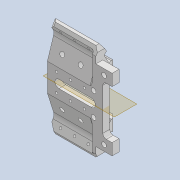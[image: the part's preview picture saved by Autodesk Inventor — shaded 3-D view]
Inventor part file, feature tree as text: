
AUTODESK INVENTOR PART (.ipt)
format: ipt  version: 2020 (Build 240168000, 168)  size: 567,808 bytes
history: native  units: mm
features: reference x17, projected_geometry x17, sketch x14, extrude x12, thicken_offset x7, fillet x7, other x5, mirror x4, plane x3, chamfer x3, hole x2
ambient origin geometry x8: Origin, YZ Plane, XZ Plane, XY Plane, X Axis, Y Axis, Z Axis, Center Point
bodies: Solid1 (feature_tree)
feature tree (91):
  sketch  "Sketch1"  dims[d0=5.0mm d1=7.0mm]
  plane  "Work Plane1"
  extrude  "Extrusion1"  Depth=7.0mm
  sketch  "Sketch2"  dims[d2=5.0mm d3=7.0mm]
  plane  "Work Plane2"
  extrude  "Extrusion2"  Depth=7.0mm
  hole  "Hole1"  [1 undecoded]
  plane  "Work Plane3"
  mirror  "Mirror1"
  extrude  "Extrusion3"  Depth=10.0mm
  thicken_offset  "Thicken1"
  thicken_offset  "Thicken2"
  thicken_offset  "Thicken3"
  extrude  "Extrusion4"  Depth=10.0mm
  extrude  "Extrusion5"  Depth=20.0mm TaperAngle=0.0deg
  thicken_offset  "Thicken4"
  thicken_offset  "Thicken5"
  extrude  "Extrusion6"  Depth=1.0mm
  extrude  "Extrusion7"  Depth=1.0mm
  fillet  "Fillet2"  Radius=1.0mm
  fillet  "Fillet3"  Radius=1.0mm
  fillet  "Fillet4"  Radius=2.9mm
  thicken_offset  "Thicken6"
  thicken_offset  "Thicken7"
  fillet  "Fillet5"  Radius=1.45mm
  chamfer  "Chamfer1"  Distance=21.5mm
  extrude  "Extrusion8"  Depth=1.0mm
  fillet  "Fillet6"  Radius=1.0mm
  chamfer  "Chamfer2"  Distance=20.0mm
  extrude  "Extrusion9"  Depth=1.5mm
  fillet  "Fillet7"  Radius=0.5mm
  mirror  "Mirror2"
  hole  "Hole2"  [1 undecoded]
  extrude  "Extrusion10"  Depth=1.5mm TaperAngle=0.0deg
  extrude  "Extrusion11"  Depth=0.1mm TaperAngle=0.0deg
  mirror  "Mirror3"
  extrude  "Extrusion12"  Depth=0.4mm
  mirror  "Mirror4"
  chamfer  "Chamfer3"  Distance=0.6mm
  fillet  "Fillet8"  Radius=1.0mm
  reference  "Reference1"
  reference  "Reference2"
  reference  "Reference3"
  reference  "Reference4"
  reference  "Reference5"
  reference  "Reference6"
  reference  "Reference7"
  reference  "Reference8"
  reference  "Reference9"
  reference  "Reference10"
  reference  "Reference11"
  reference  "Reference12"
  reference  "Reference13"
  reference  "Reference14"
  projected_geometry  "Projected Loop1"
  sketch  "Sketch3"  dims[d4=3.0mm d5=21.0mm]
  reference  "Reference15"
  reference  "Reference16"
  reference  "Reference17"
  sketch  "Sketch4"  dims[d6=10.0mm d7=0.0mm d8=2.0mm]
  projected_geometry  "Projected Loop2"
  projected_geometry  "Projected Loop3"
  sketch  "Sketch5"  dims[d9=10.0mm d10=0.0mm]
  projected_geometry  "Projected Loop4"
  sketch  "Sketch6"  dims[d11=1.1mm d12=6.0mm d13=4.0mm d14=2.0mm d15=90.0deg d16=10.0mm d17=0.0mm d18=2.0mm]
  projected_geometry  "Projected Loop5"
  projected_geometry  "Projected Loop6"
  projected_geometry  "Projected Loop7"
  sketch  "Sketch7"  dims[d19=2.0mm d20=20.0mm d21=0.0mm]
  projected_geometry  "Projected Loop8"
  projected_geometry  "Projected Loop9"
  sketch  "Sketch8"  dims[d22=1.0mm d23=1.0mm]
  projected_geometry  "Projected Loop10"
  sketch  "Sketch9"  dims[d24=1.0mm d25=1.0mm d26=1.0mm d27=1.0mm d28=2.9mm d29=1.45mm]
  projected_geometry  "Projected Loop11"
  projected_geometry  "Projected Loop12"
  sketch  "Sketch10"  dims[d30=2.9mm]
  projected_geometry  "Projected Loop13"
  sketch  "Sketch11"  dims[d31=12.0mm d32=21.5mm d33=0.0mm]
  projected_geometry  "Projected Loop14"
  sketch  "Sketch12"  dims[d35=1.0mm d36=1.0mm d37=1.0mm]
  projected_geometry  "Projected Loop15"
  sketch  "Sketch13"  dims[d38=1.0mm d39=20.0mm d40=0.0mm]
  projected_geometry  "Projected Loop16"
  sketch  "Sketch14"  dims[d41=0.5mm d42=0.5mm d43=0.5mm d44=0.5mm d45=20.0mm d46=0.0mm d47=0.1mm d48=0.0mm d49=0.4mm d50=0.6mm d51=1.0mm d52=0.5mm d53=0.5mm d54=0.5mm d55=0.5mm d56=3.0mm d57=1.5mm d58=2.0mm d59=45.0deg d60=2.0mm d61=0.0mm d62=1.0mm d63=1.5mm d64=2.0mm d65=45.0deg d66=3.5mm d67=3.5mm d68=1.5mm d69=30.0mm d70=0.0mm d71=1.0mm d72=4.0mm d73=6.0mm d74=6.0mm d75=4.0mm d76=4.0mm d77=4.0mm d78=4.0mm d79=4.0mm d80=4.0mm d81=1.1mm d82=6.0mm d83=4.0mm d84=2.0mm d85=90.0deg d86=10.0mm d87=0.0mm d88=7.0mm d89=3.5mm d90=30.0mm d91=0.0mm d92=4.0mm d93=1.0mm d94=2.0mm d95=30.0mm d96=0.0mm d97=5.0mm d98=8.0mm d99=2.0mm d100=2.0mm d101=30.0mm d102=0.0mm d103=2.0mm d104=2.0mm d105=45.0deg d106=1.5mm]
  projected_geometry  "Projected Loop17"
  parser-record x1  (decoder bookkeeping rows leaked as tree rows — omitted from the tree; the rows remain in map.json)
  other  "tip_3_n_ass.iam"
  other  "end_shell_n_1:1"
  other  "bl_tube_ass_2:1"
  other  "bl_tube_hn_1:1"
note: 2 required parameter values undecoded (feature->parameter linkage not recoverable at this tier; creation-order binding heuristic only, values carry confidence <= 0.55)
note: 1 file-system path scrubbed to <path> (originals preserved in map.json)
